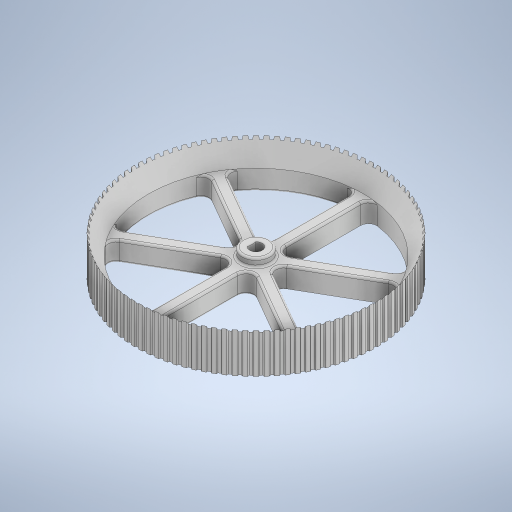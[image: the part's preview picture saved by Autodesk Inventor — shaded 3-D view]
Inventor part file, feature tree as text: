
AUTODESK INVENTOR PART (.ipt)
format: ipt  version: 2024.2 (Build 282272000, 272)  size: 1,124,352 bytes
history: native  units: mm
features: sketch x3, extrude x3, fillet x2, revolve x1
ambient origin geometry x8: Origin, YZ Plane, XZ Plane, XY Plane, X Axis, Y Axis, Z Axis, Center Point
bodies: Solid1 (feature_tree)
feature tree (9):
  revolve  "Revolution1"  [1 undecoded]
  sketch  "Sketch3"  dims[d2=5.0mm d3=30.0mm]
  extrude  "Extrusion1"  Depth=30.0mm
  extrude  "Extrusion2"  Depth=0.5mm
  extrude  "Extrusion3"  Depth=0.5mm
  fillet  "Fillet1"  Radius=5.0mm
  fillet  "Fillet2"  Radius=7.0mm
  sketch  "Sketch2"  dims[d0=3.0mm d1=10.0mm]
  sketch  "Sketch4"  dims[d4=90.0deg d5=3.15mm d6=1.15mm d7=5.0mm d8=7.0mm d9=3.0mm d10=1.5mm d11=60.0mm d13=360.0deg d15=5.0mm d16=0.0mm d17=7.0mm d18=0.0mm d19=120.0deg d20=120.0deg d21=1.6mm d22=1.0mm d23=0.5mm d24=1000.0mm d26=360.0deg d28=0.0mm d29=0.0mm d30=2.0mm d31=0.5mm d32=0.0mm d33=0.0mm d34=0.0mm d35=0.0mm]
note: 1 required parameter value undecoded (feature->parameter linkage not recoverable at this tier; creation-order binding heuristic only, values carry confidence <= 0.55)
